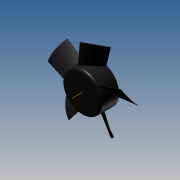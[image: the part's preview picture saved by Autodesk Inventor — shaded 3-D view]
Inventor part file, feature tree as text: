
AUTODESK INVENTOR PART (.ipt)
format: ipt  version: 2013 (Build 170138000, 138)  size: 170,496 bytes
history: native  units: mm (DEFAULTED — no unit token found)
features: sketch x6, extrude x3, plane x3, fillet x1, loft x1, other x1, pattern_circular x1
ambient origin geometry x8: Origin, YZ Plane, XZ Plane, XY Plane, X Axis, Y Axis, Z Axis, Center Point
bodies: Solid1 (feature_tree)
feature tree (16):
  extrude  "Extrusion1"  Depth=26.416mm TaperAngle=0.0deg
  fillet  "Fillet1"  Radius=3.175mm
  sketch  "Sketch2"  dims[d5=38.1mm d6=-12.7mm]
  plane  "Work Plane1"
  plane  "Work Plane2"
  sketch  "Sketch4"  dims[d7=0.0mm d8=90.0deg]
  plane  "Work Plane3"
  loft  "Loft1"
  other  "Work Axis1"
  pattern_circular  "Circular Pattern1"  Count=5 Angle=360.0deg
  extrude  "Extrusion2"  Depth=1.27mm
  extrude  "Extrusion3"  Depth=22.225mm TaperAngle=0.0deg
  sketch  "Sketch1"  dims[d0=57.785mm d1=26.416mm d2=0.0mm d3=3.175mm]
  sketch  "Sketch5"  dims[d9=0.0mm d10=90.0deg]
  sketch  "Sketch6"  dims[d11=114.3mm]
  sketch  "Sketch7"  dims[d12=26.416mm d13=0.0mm d14=50.0mm d16=360.0deg d17=1.27mm d18=22.225mm d19=0.0mm]
